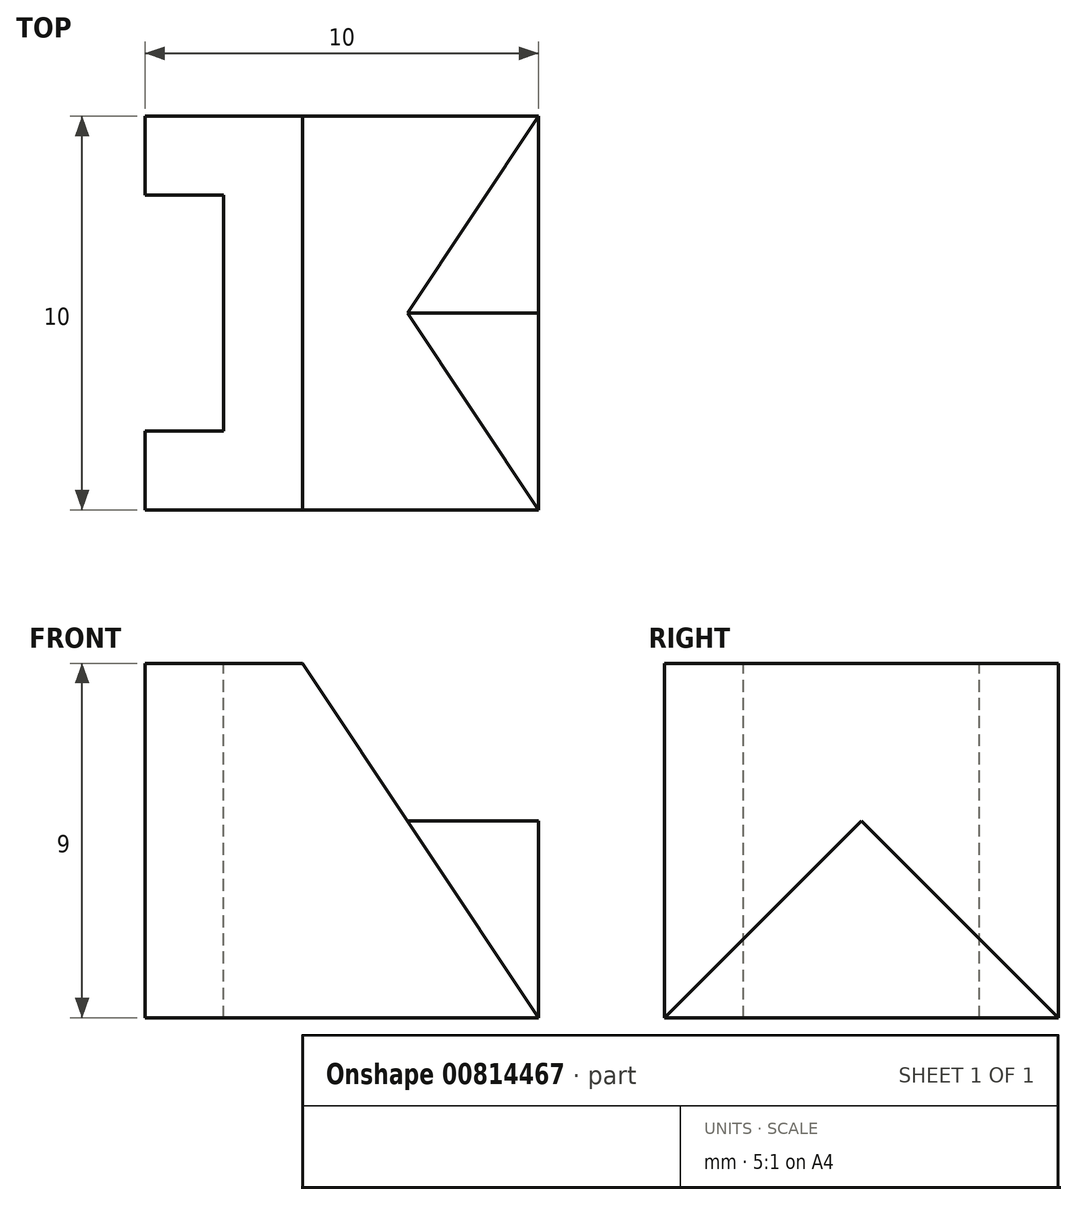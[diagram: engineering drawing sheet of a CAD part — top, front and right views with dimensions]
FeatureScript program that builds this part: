
annotation { "Feature Type Name" : "Feature", "Feature Type Description" : "" }
export const myFeature = defineFeature(function(context is Context, id is Id, definition is map)
    precondition{}
    {
        {
            var Q0;
            Q0=qCreatedBy(makeId("Front.planeOp"),FACE);
            var sketch = newSketch(context, id + "F0", { "sketchPlane" : qUnion([Q0])});
            skLineSegment(sketch, "E0", {"start": v(-10, 9) * mm, "end": v(-10, 0) * mm});
            skLineSegment(sketch, "E1", {"start": v(-10, 0) * mm, "end": v(0, 0) * mm});
            skLineSegment(sketch, "E2", {"start": v(-10, 9) * mm, "end": v(-6, 9) * mm});
            skLineSegment(sketch, "E3", {"start": v(-6, 9) * mm, "end": v(0, 0) * mm});
            skSolve(sketch);
        }
        {
            var Q0;
            Q0 = qSketchRegion(id + "F0", true);
            extrude(context, id + "F1", {"entities" : qUnion([Q0]), "oppositeDirection" : true, "depth" : 10 * mm, "offsetDistance" : 25 * mm});
        }
        {
            var Q0;
            Q0=makeQuery(id+"F1.opExtrude","SWEPT_FACE",FACE,{"disambiguationData":[OSD([sQuery(id+"F0.wireOp",EDGE,"E2")])]});
            var sketch = newSketch(context, id + "F2", { "sketchPlane" : qUnion([Q0])});
            skLineSegment(sketch, "E4.bottom", {"start": v(-10, 8) * mm, "end": v(-8, 8) * mm});
            skLineSegment(sketch, "E4.top", {"start": v(-10, 2) * mm, "end": v(-8, 2) * mm});
            skLineSegment(sketch, "E4.left", {"start": v(-10, 8) * mm, "end": v(-10, 2) * mm});
            skLineSegment(sketch, "E4.right", {"start": v(-8, 8) * mm, "end": v(-8, 2) * mm});
            skSolve(sketch);
        }
        {
            var Q0;
            Q0 = qSketchRegion(id + "F2", true);
            extrude(context, id + "F3", {"entities" : qUnion([Q0]), "operationType" : NewBodyOperationType.REMOVE, "endBound" : BoundingType.THROUGH_ALL, "oppositeDirection" : true, "depth" : 25 * mm, "offsetDistance" : 25 * mm});
        }
        {
            var Q0;
            Q0=qCreatedBy(makeId("Right.planeOp"),FACE);
            var sketch = newSketch(context, id + "F4", { "sketchPlane" : qUnion([Q0])});
            skLineSegment(sketch, "E5.0", {"start": v(10, 0) * mm, "end": v(0, 0) * mm});
            skLineSegment(sketch, "E6", {"start": v(0, 0) * mm, "end": v(5, 5) * mm});
            skPoint(sketch, "E6.endSnap0", {"position": v(5, 0) * mm});
            skLineSegment(sketch, "E7", {"start": v(5, 5) * mm, "end": v(10, 0) * mm});
            skSolve(sketch);
        }
        {
            var Q0;
            Q0 = qSketchRegion(id + "F4", true);
            var Q1;
            Q1=makeQuery(id+"F1.opExtrude","SWEPT_FACE",FACE,{"disambiguationData":[OSD([sQuery(id+"F0.wireOp",EDGE,"E3")])]});
            extrude(context, id + "F5", {"entities" : qUnion([Q0]), "operationType" : NewBodyOperationType.ADD, "endBound" : BoundingType.UP_TO_SURFACE, "oppositeDirection" : true, "depth" : 25 * mm, "endBoundEntityFace" : qUnion([Q1]), "offsetDistance" : 25 * mm});
        }
    });
